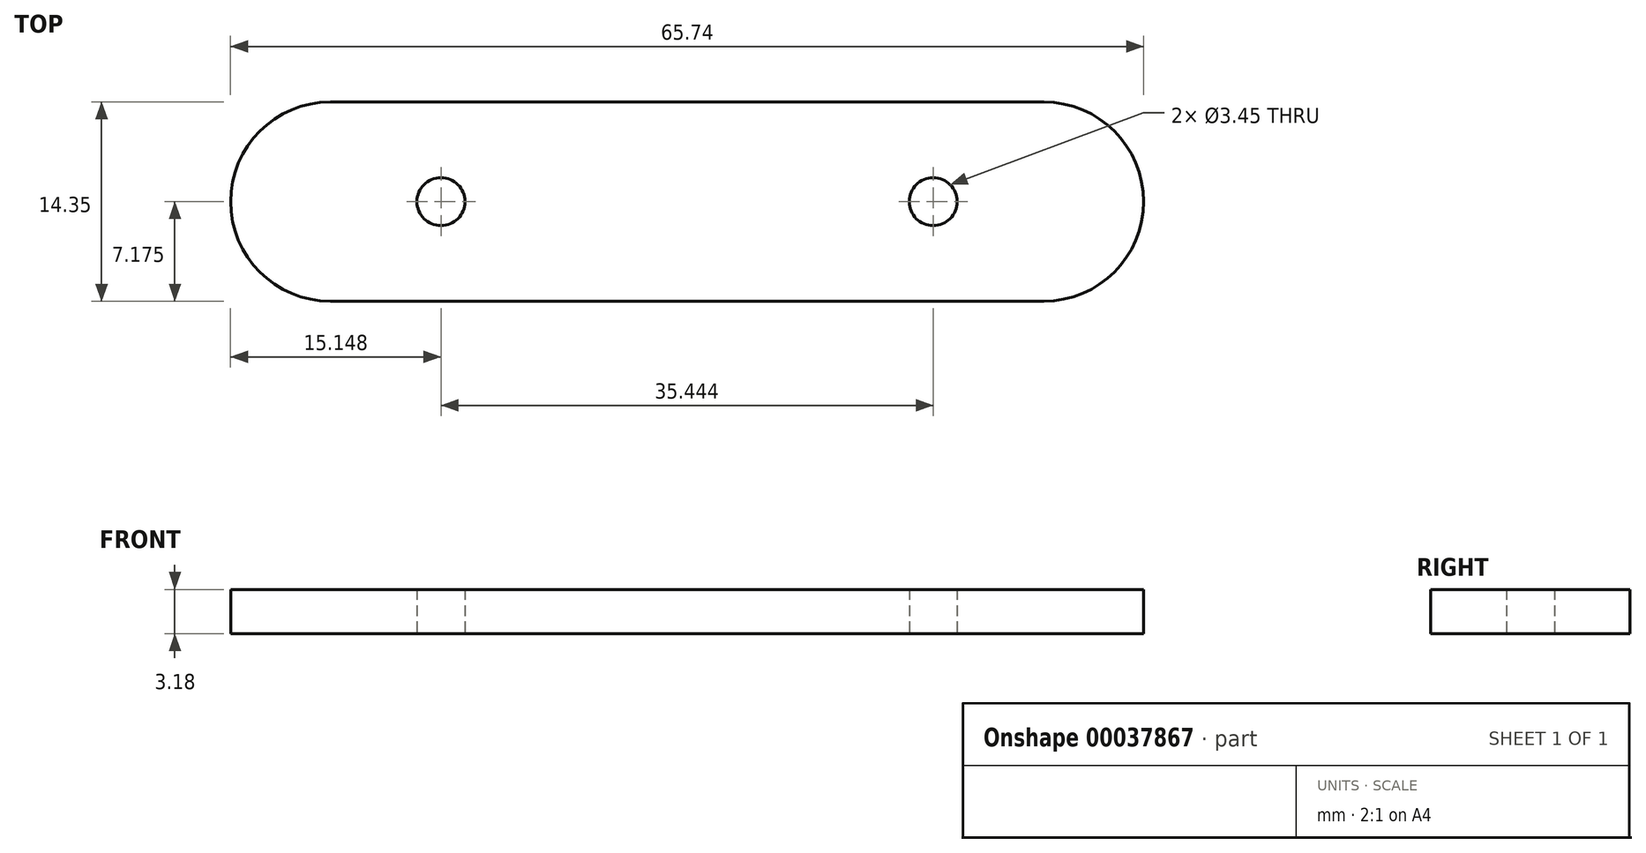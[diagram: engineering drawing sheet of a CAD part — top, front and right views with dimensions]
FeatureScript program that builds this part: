
annotation { "Feature Type Name" : "Feature", "Feature Type Description" : "" }
export const myFeature = defineFeature(function(context is Context, id is Id, definition is map)
    precondition{}
    {
        {
            var Q0;
            Q0=qCreatedBy(makeId("Top.planeOp"),FACE);
            var sketch = newSketch(context, id + "F0", { "sketchPlane" : qUnion([Q0])});
            skLineSegment(sketch, "E0", {"start": v(17.72, -7.18) * mm, "end": v(-17.72, -7.18) * mm, "construction": true});
            skCircle(sketch, "E1", {"center": v(-25.7, -7.18) * mm, "radius": 4 * mm, "construction": true});
            skLineSegment(sketch, "E2", {"start": v(0, 0) * mm, "end": v(0, -7.18) * mm, "construction": true});
            skLineSegment(sketch, "E3", {"start": v(-17.72, -7.18) * mm, "end": v(-25.7, -7.18) * mm, "construction": true});
            skCircle(sketch, "E4", {"center": v(-17.72, -7.18) * mm, "radius": 1.73 * mm});
            skLineSegment(sketch, "E5", {"start": v(25.7, -7.18) * mm, "end": v(17.72, -7.18) * mm, "construction": true});
            skCircle(sketch, "E6", {"center": v(25.7, -7.18) * mm, "radius": 4 * mm, "construction": true});
            skCircle(sketch, "E7", {"center": v(17.72, -7.18) * mm, "radius": 1.73 * mm});
            skCircle(sketch, "E8", {"center": v(17.72, -7.18) * mm, "radius": 3.97 * mm, "construction": true});
            skLineSegment(sketch, "E9.bottom", {"start": v(-25.7, 0) * mm, "end": v(25.7, 0) * mm});
            skLineSegment(sketch, "E9.top", {"start": v(-25.7, -14.35) * mm, "end": v(25.7, -14.35) * mm});
            skLineSegment(sketch, "E9.left", {"start": v(-25.7, 0) * mm, "end": v(-25.7, -14.35) * mm, "construction": true});
            skLineSegment(sketch, "E9.right", {"start": v(25.7, 0) * mm, "end": v(25.7, -14.35) * mm, "construction": true});
            skArc(sketch, "E10", {"start": v(-25.7, 0) * mm, "mid": v(-32.87, -7.18) * mm, "end": v(-25.7, -14.35) * mm});
            skArc(sketch, "E11", {"start": v(25.7, -14.35) * mm, "mid": v(32.87, -7.18) * mm, "end": v(25.7, 0) * mm});
            skSolve(sketch);
        }
        {
            var Q0;
            Q0 = qSketchRegion(id + "F0", true);
            extrude(context, id + "F1", {"entities" : qUnion([Q0]), "depth" : 3.17 * mm});
        }
    });
